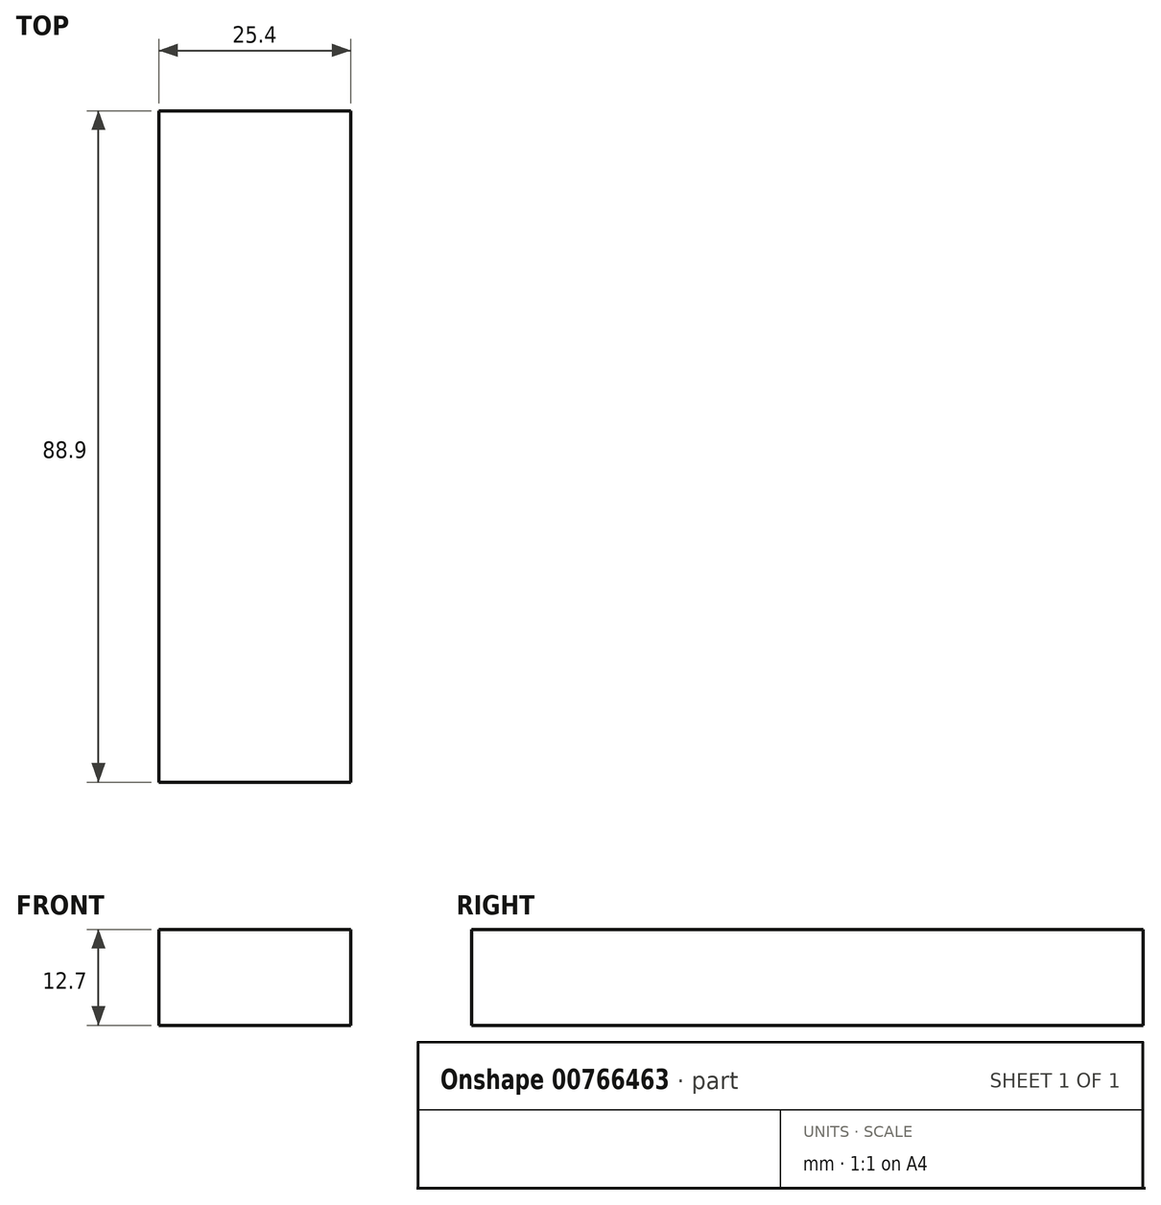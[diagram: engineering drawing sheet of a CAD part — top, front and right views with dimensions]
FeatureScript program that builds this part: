
annotation { "Feature Type Name" : "Feature", "Feature Type Description" : "" }
export const myFeature = defineFeature(function(context is Context, id is Id, definition is map)
    precondition{}
    {
        {
            var Q0;
            Q0=qCreatedBy(makeId("Front.planeOp"),FACE);
            var sketch = newSketch(context, id + "F0", { "sketchPlane" : qUnion([Q0])});
            skLineSegment(sketch, "E0.bottom", {"start": v(57.27, 45.08) * mm, "end": v(31.87, 45.08) * mm});
            skLineSegment(sketch, "E0.top", {"start": v(57.27, 32.38) * mm, "end": v(31.87, 32.38) * mm});
            skLineSegment(sketch, "E0.left", {"start": v(57.27, 45.08) * mm, "end": v(57.27, 32.38) * mm});
            skLineSegment(sketch, "E0.right", {"start": v(31.87, 45.08) * mm, "end": v(31.87, 32.38) * mm});
            skSolve(sketch);
        }
        {
            var Q0;
            Q0=qSketchRegion(id+"F0",true);
            extrude(context, id + "F1", {"entities" : qUnion([Q0]), "depth" : 88.9 * mm, "offsetDistance" : 25.4 * mm});
        }
    });
